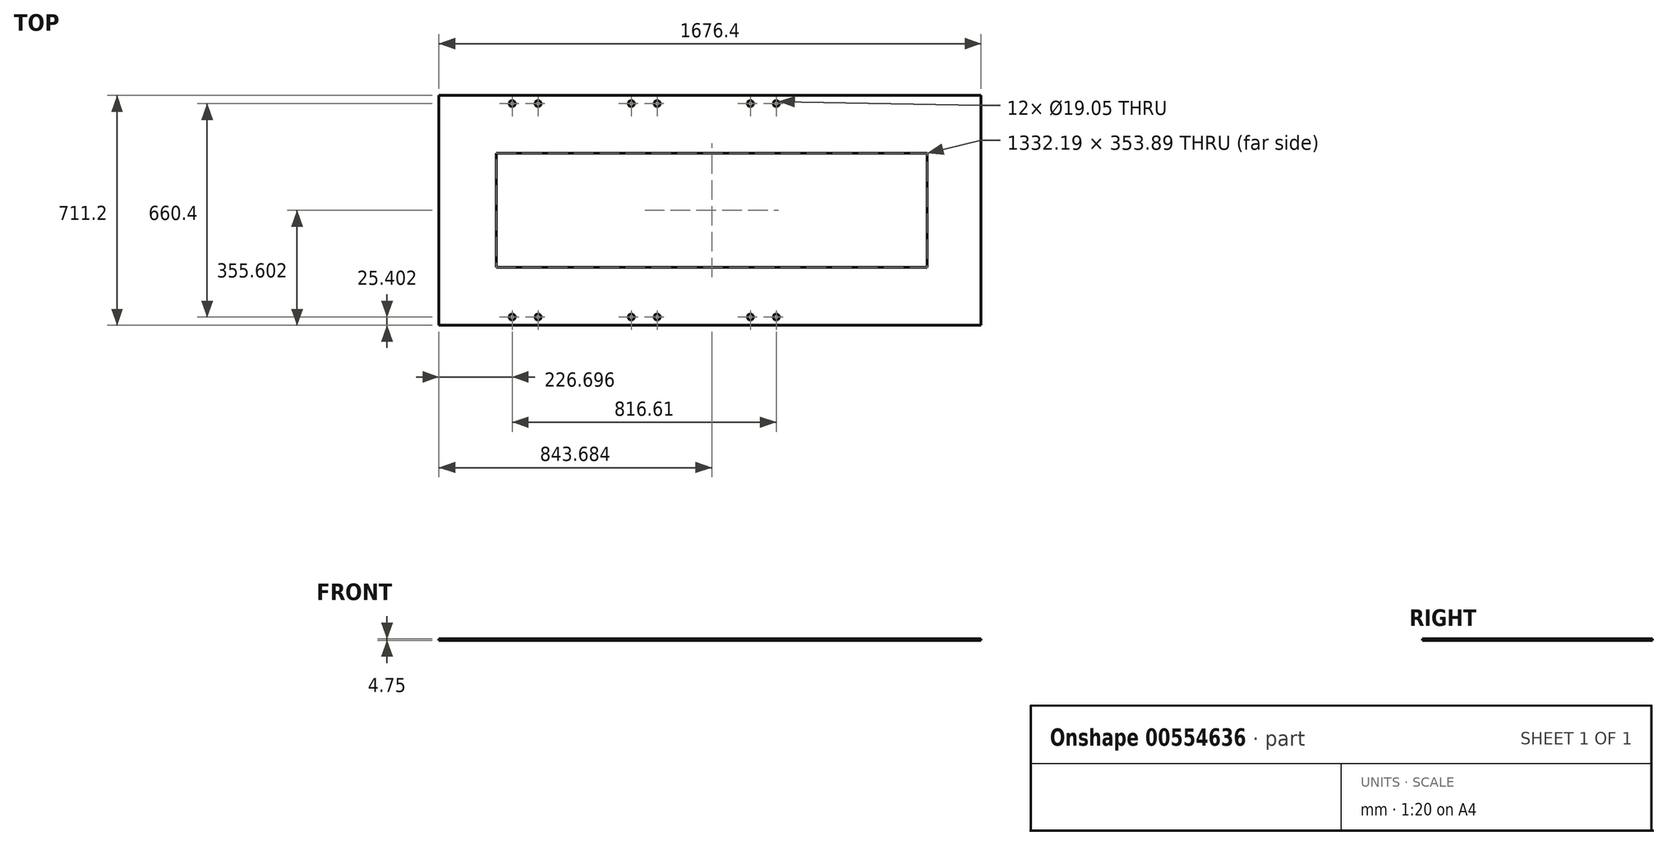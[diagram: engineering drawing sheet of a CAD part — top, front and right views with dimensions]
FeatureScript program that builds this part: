
annotation { "Feature Type Name" : "Feature", "Feature Type Description" : "" }
export const myFeature = defineFeature(function(context is Context, id is Id, definition is map)
    precondition{}
    {
        {
            var Q0;
            Q0=qCreatedBy(makeId("Top.planeOp"),FACE);
            var sketch = newSketch(context, id + "F0", { "sketchPlane" : qUnion([Q0])});
            skLineSegment(sketch, "E0.bottom", {"start": v(-680.89, 207.58) * mm, "end": v(995.51, 207.58) * mm});
            skLineSegment(sketch, "E0.top", {"start": v(-680.89, -503.62) * mm, "end": v(995.51, -503.62) * mm});
            skLineSegment(sketch, "E0.left", {"start": v(-680.89, 207.58) * mm, "end": v(-680.89, -503.62) * mm});
            skLineSegment(sketch, "E0.right", {"start": v(995.51, 207.58) * mm, "end": v(995.51, -503.62) * mm});
            skLineSegment(sketch, "E1.top", {"start": v(-503.3, 28.93) * mm, "end": v(828.89, 28.93) * mm});
            skLineSegment(sketch, "E1.left", {"start": v(-503.3, -148.02) * mm, "end": v(-503.3, 28.93) * mm});
            skLineSegment(sketch, "E1.right", {"start": v(828.89, -148.02) * mm, "end": v(828.89, 28.93) * mm});
            skLineSegment(sketch, "E2.MirrorCS", {"start": v(-503.3, -324.96) * mm, "end": v(828.89, -324.96) * mm});
            skLineSegment(sketch, "E3.MirrorCS", {"start": v(-503.3, -148.02) * mm, "end": v(-503.3, -324.96) * mm});
            skLineSegment(sketch, "E4.MirrorCS", {"start": v(828.89, -148.02) * mm, "end": v(828.89, -324.96) * mm});
            skLineSegment(sketch, "E5.MirrorCS", {"start": v(-680.89, -503.62) * mm, "end": v(-680.89, 207.58) * mm});
            skCircle(sketch, "E6", {"center": v(-454.2, 182.18) * mm, "radius": 9.53 * mm});
            skCircle(sketch, "E7.MirrorC", {"center": v(-374.18, 182.18) * mm, "radius": 9.53 * mm});
            skCircle(sketch, "E8.MirrorC", {"center": v(362.42, 182.18) * mm, "radius": 9.53 * mm});
            skCircle(sketch, "E9", {"center": v(-85.9, 182.18) * mm, "radius": 9.53 * mm});
            skCircle(sketch, "E10.MirrorC", {"center": v(-5.88, 182.18) * mm, "radius": 9.53 * mm});
            skCircle(sketch, "E11.MirrorC", {"center": v(282.4, 182.18) * mm, "radius": 9.53 * mm});
            skCircle(sketch, "E12.MirrorC", {"center": v(-454.2, -478.22) * mm, "radius": 9.53 * mm});
            skCircle(sketch, "E13.MirrorC", {"center": v(-374.18, -478.22) * mm, "radius": 9.53 * mm});
            skCircle(sketch, "E14.MirrorC", {"center": v(-85.9, -478.22) * mm, "radius": 9.53 * mm});
            skCircle(sketch, "E15.MirrorC", {"center": v(-5.88, -478.22) * mm, "radius": 9.53 * mm});
            skCircle(sketch, "E16.MirrorC", {"center": v(282.4, -478.22) * mm, "radius": 9.53 * mm});
            skCircle(sketch, "E17.MirrorC", {"center": v(362.42, -478.22) * mm, "radius": 9.53 * mm});
            skPoint(sketch, "E18.MirrorCS.end.orphan", {"position": v(-414.19, 28.93) * mm});
            skPoint(sketch, "E18.MirrorCS.start.orphan", {"position": v(-414.19, 207.58) * mm});
            skPoint(sketch, "E19.end.orphan", {"position": v(-45.89, 28.93) * mm});
            skPoint(sketch, "E19.start.orphan", {"position": v(-45.89, 207.58) * mm});
            skPoint(sketch, "E20.end.orphan", {"position": v(322.41, 28.93) * mm});
            skPoint(sketch, "E20.start.orphan", {"position": v(322.41, 207.58) * mm});
            skPoint(sketch, "E21.MirrorCS.end.orphan", {"position": v(322.41, -324.96) * mm});
            skPoint(sketch, "E21.MirrorCS.start.orphan", {"position": v(322.41, -503.62) * mm});
            skPoint(sketch, "E22.MirrorCS.end.orphan", {"position": v(-45.89, -324.96) * mm});
            skPoint(sketch, "E22.MirrorCS.start.orphan", {"position": v(-45.89, -503.62) * mm});
            skPoint(sketch, "E23.MirrorCS.end.orphan", {"position": v(-414.19, -324.96) * mm});
            skPoint(sketch, "E23.MirrorCS.start.orphan", {"position": v(-414.19, -503.62) * mm});
            skSolve(sketch);
        }
        {
            var Q0;
            Q0=makeQuery(id+"F0.imprint","IMPRINT",FACE,{"disambiguationData":[TD([[makeQuery(id+"F0.imprint","IMPRINT",EDGE,{"derivedFrom":sQuery(id+"F0.wireOp",EDGE,"E0.bottom")}),-1.0]])]});
            extrude(context, id + "F1", {"entities" : qUnion([Q0]), "depth" : 4.75 * mm, "offsetDistance" : 25.4 * mm});
        }
    });
